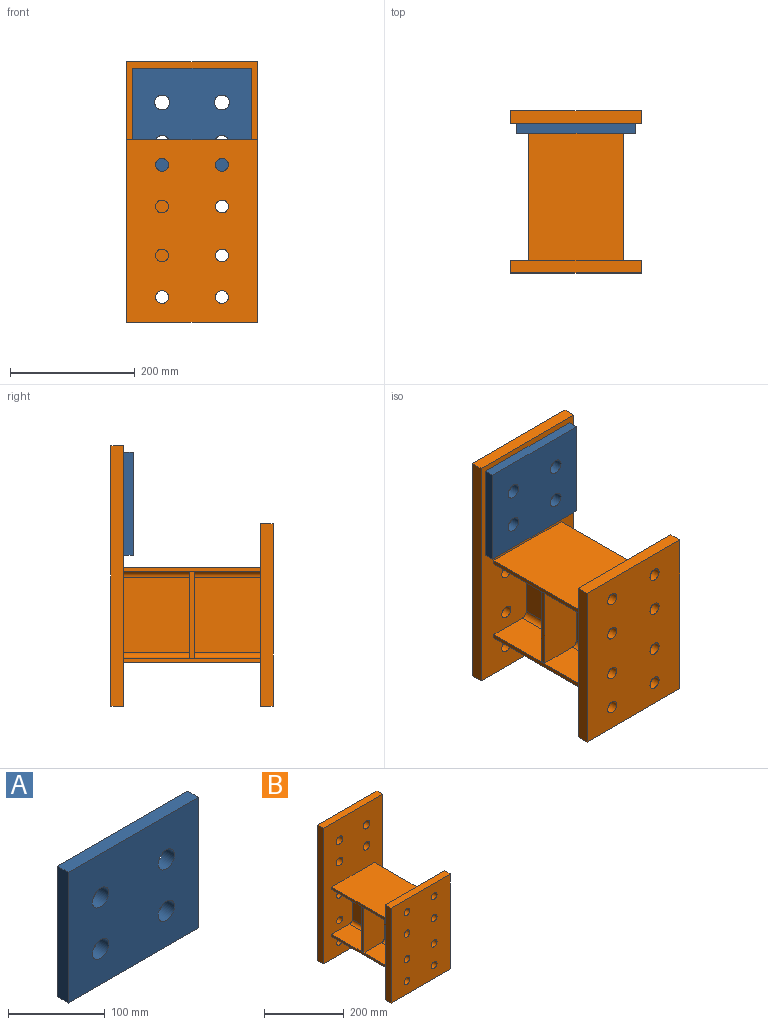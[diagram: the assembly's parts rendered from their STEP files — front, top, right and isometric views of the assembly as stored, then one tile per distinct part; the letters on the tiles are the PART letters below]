
ASSEMBLY  parts=2 mates=1
PART A: 10 faces, bbox 190x16x165 mm
  f0: plane 190x16mm, normal (0,0,-1), area 3040mm2, adj f1,f7,f8,f9
  f1: plane 165x16mm, normal (1,0,0), area 2640mm2, adj f0,f2,f8,f9
  f2: plane 190x16mm, normal (0,0,1), area 3040mm2, adj f1,f7,f8,f9
  f3: cylinder r=12mm len=24mm, axis (0,1,0), area 1206.4mm2, adj f8,f9
  f4: cylinder r=12mm len=24mm, axis (0,1,0), area 1206.4mm2, adj f8,f9
  f5: cylinder r=12mm len=24mm, axis (0,1,0), area 1206.4mm2, adj f8,f9
  f6: cylinder r=12mm len=24mm, axis (0,1,0), area 1206.4mm2, adj f8,f9
  f7: plane 165x16mm, normal (-1,0,0), area 2640mm2, adj f0,f2,f8,f9
  f8: plane 190x165mm, normal (0,-1,0), area 29540.4mm2, adj f0,f1,f2,f3,f4,f5,f6,f7
  f9: plane 190x165mm, normal (0,1,0), area 29540.4mm2, adj f0,f1,f2,f3,f4,f5,f6,f7
PART B: 52 faces, bbox 210x260x417 mm
  f0: cylinder r=8.9mm len=106mm, axis (0,1,0), area 1481.9mm2, adj f1,f4,f19,f35
  f1: plane 220x64.05mm, normal (0,0,1), area 13586.2mm2, adj f0,f5,f6,f19,f20,f21,f35,f36
  f2: plane 220x64.05mm, normal (0,0,-1), area 13586.2mm2, adj f3,f16,f17,f19,f20,f21,f35,f36
  f3: cylinder r=8.9mm len=106mm, axis (0,1,0), area 1481.9mm2, adj f2,f4,f19,f35
  f4: plane 120.6x106mm, normal (-1,0,0), area 12783.6mm2, adj f0,f3,f19,f35
  f5: cylinder r=8.9mm len=106mm, axis (0,1,0), area 1481.9mm2, adj f1,f18,f20,f36
  f6: plane 220x6.8mm, normal (-1,0,0), area 1496mm2, adj f1,f7,f35,f36
  f7: plane 220x152mm, normal (0,0,-1), area 33440mm2, adj f6,f8,f35,f36
  f8: plane 220x6.8mm, normal (1,0,0), area 1496mm2, adj f7,f9,f35,f36
  f9: plane 220x64.05mm, normal (0,0,1), area 14091mm2, adj f8,f10,f35,f36
  f10: cylinder r=8.9mm len=220mm, axis (0,1,0), area 3075.6mm2, adj f9,f11,f35,f36
  f11: plane 220x120.6mm, normal (1,0,0), area 26532mm2, adj f10,f12,f35,f36
  f12: cylinder r=8.9mm len=220mm, axis (0,1,0), area 3075.6mm2, adj f11,f13,f35,f36
  f13: plane 220x64.05mm, normal (0,0,-1), area 14091mm2, adj f12,f14,f35,f36
  f14: plane 220x6.8mm, normal (1,0,0), area 1496mm2, adj f13,f15,f35,f36
  f15: plane 220x152mm, normal (0,0,1), area 33440mm2, adj f14,f16,f35,f36
  f16: plane 220x6.8mm, normal (-1,0,0), area 1496mm2, adj f2,f15,f35,f36
  f17: cylinder r=8.9mm len=106mm, axis (0,1,0), area 1481.9mm2, adj f2,f18,f20,f36
  f18: plane 120.6x106mm, normal (-1,0,0), area 12783.6mm2, adj f5,f17,f20,f36
  f19: plane 138.4x72mm, normal (0,-1,0), area 9930.8mm2, adj f0,f1,f2,f3,f4,f21
  f20: plane 138.4x72mm, normal (0,1,0), area 9930.8mm2, adj f1,f2,f5,f17,f18,f21
  f21: plane 138.4x8mm, normal (-1,0,0), area 1107.2mm2, adj f1,f2,f19,f20
  f22: plane 292x20mm, normal (1,0,0), area 5840mm2, adj f23,f26,f34,f35
  f23: plane 210x20mm, normal (0,0,1), area 4200mm2, adj f22,f24,f34,f35
  f24: plane 292x20mm, normal (-1,0,0), area 5840mm2, adj f23,f26,f34,f35
  f25: cylinder r=10.25mm len=20.5mm, axis (0,1,0), area 1288.1mm2, adj f34,f35
  f26: plane 210x20mm, normal (0,0,-1), area 4200mm2, adj f22,f24,f34,f35
  f27: cylinder r=10.25mm len=20.5mm, axis (0,1,0), area 1288.1mm2, adj f34,f35
  f28: cylinder r=10.25mm len=20.5mm, axis (0,1,0), area 1288.1mm2, adj f34,f35
  f29: cylinder r=10.25mm len=20.5mm, axis (0,1,0), area 1288.1mm2, adj f34,f35
  f30: cylinder r=10.25mm len=20.5mm, axis (0,1,0), area 1288.1mm2, adj f34,f35
  f31: cylinder r=10.25mm len=20.5mm, axis (0,1,0), area 1288.1mm2, adj f34,f35
  f32: cylinder r=10.25mm len=20.5mm, axis (0,1,0), area 1288.1mm2, adj f34,f35
  f33: cylinder r=10.25mm len=20.5mm, axis (0,1,0), area 1288.1mm2, adj f34,f35
  f34: plane 292x210mm, normal (0,-1,0), area 58679.5mm2, adj f22,f23,f24,f25,f26,f27,f28,f29
  f35: plane 292x210mm, normal (0,1,0), area 55700.1mm2, adj f0,f1,f2,f3,f4,f6,f7,f8
  f36: plane 417x210mm, normal (0,-1,0), area 80800.6mm2, adj f1,f2,f5,f6,f7,f8,f9,f10
  f37: plane 210x20mm, normal (0,0,1), area 4200mm2, adj f36,f38,f45,f51
  f38: plane 417x20mm, normal (1,0,0), area 8340mm2, adj f36,f37,f39,f51
  f39: plane 210x20mm, normal (0,0,-1), area 4200mm2, adj f36,f38,f45,f51
  f40: cylinder r=10.25mm len=20.5mm, axis (0,-1,0), area 1288.1mm2, adj f36,f51
  f41: cylinder r=10.25mm len=20.5mm, axis (0,-1,0), area 1288.1mm2, adj f36,f51
  f42: cylinder r=10.25mm len=20.5mm, axis (0,-1,0), area 1288.1mm2, adj f36,f51
  f43: cylinder r=10.25mm len=20.5mm, axis (0,-1,0), area 1288.1mm2, adj f36,f51
  f44: cylinder r=10.25mm len=20.5mm, axis (0,-1,0), area 1288.1mm2, adj f36,f51
  f45: plane 417x20mm, normal (-1,0,0), area 8340mm2, adj f36,f37,f39,f51
  f46: cylinder r=10.25mm len=20.5mm, axis (0,-1,0), area 1288.1mm2, adj f36,f51
  f47: cylinder r=12mm len=24mm, axis (0,-1,0), area 1508mm2, adj f36,f51
  f48: cylinder r=12mm len=24mm, axis (0,-1,0), area 1508mm2, adj f36,f51
  f49: cylinder r=12mm len=24mm, axis (0,-1,0), area 1508mm2, adj f36,f51
  f50: cylinder r=12mm len=24mm, axis (0,-1,0), area 1508mm2, adj f36,f51
  f51: plane 417x210mm, normal (0,1,0), area 83780.1mm2, adj f37,f38,f39,f40,f41,f42,f43,f44
PLACE A t=(-118.92,73.81,176.7)mm
PLACE B t=(-118.92,-28.19,-1.8)mm
MATE fastened A.f4 <-> B.f50  axis (0,1,0) through (-166.92,81.81,204.2)mm
